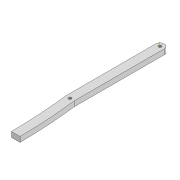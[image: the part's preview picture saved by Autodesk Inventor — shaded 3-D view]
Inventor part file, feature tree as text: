
AUTODESK INVENTOR PART (.ipt)
format: ipt  version: 2022 (Build 260153000, 153)  size: 108,032 bytes
history: native  units: mm
features: extrude x2, sketch x2, other x1
ambient origin geometry x8: Origin, YZ Plane, XZ Plane, XY Plane, X Axis, Y Axis, Z Axis, Center Point
bodies: Solid1 (feature_tree)
feature tree (5):
  extrude  "Extrusion1"  Depth=3.3mm
  other  "Work Axis3"
  extrude  "Extrusion2"  Depth=322.934mm
  sketch  "Sketch1"  dims[d0=3.3mm d1=3.3mm]
  sketch  "Sketch2"  dims[d2=10.0mm d3=322.934mm d4=3.3mm d5=74.182mm d6=6.0mm d7=0.0mm d8=3.3mm d9=218.733mm d12=600.0mm d13=600.0mm d14=100.0mm d15=0.0mm]
